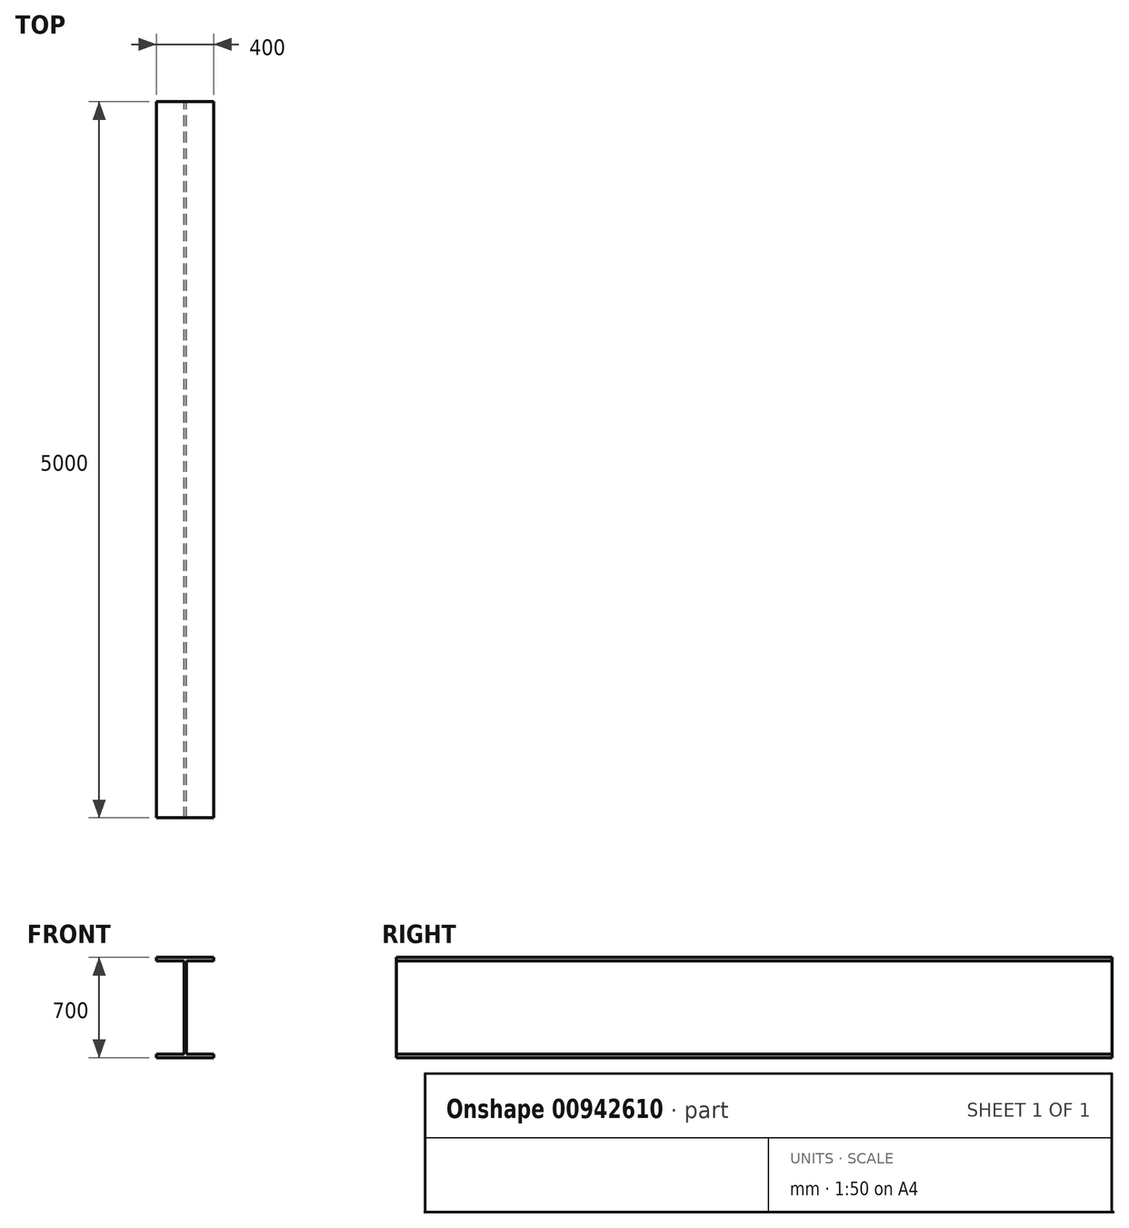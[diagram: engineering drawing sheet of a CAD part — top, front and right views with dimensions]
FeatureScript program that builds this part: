
annotation { "Feature Type Name" : "Feature", "Feature Type Description" : "" }
export const myFeature = defineFeature(function(context is Context, id is Id, definition is map)
    precondition{}
    {
        {
            var Q0;
            Q0=qCreatedBy(makeId("Front.planeOp"),FACE);
            var sketch = newSketch(context, id + "F0", { "sketchPlane" : qUnion([Q0])});
            skLineSegment(sketch, "E0.bottom", {"start": v(-253.34, 352.68) * mm, "end": v(146.66, 352.68) * mm});
            skLineSegment(sketch, "E0.top", {"start": v(-253.34, 327.68) * mm, "end": v(-61.34, 327.68) * mm});
            skLineSegment(sketch, "E0.left", {"start": v(-253.34, 352.68) * mm, "end": v(-253.34, 327.68) * mm});
            skLineSegment(sketch, "E0.right", {"start": v(146.66, 352.68) * mm, "end": v(146.66, 327.68) * mm});
            skLineSegment(sketch, "E1.bottom", {"start": v(-253.34, -322.32) * mm, "end": v(-61.34, -322.32) * mm});
            skLineSegment(sketch, "E1.top", {"start": v(-253.34, -347.32) * mm, "end": v(146.66, -347.32) * mm});
            skLineSegment(sketch, "E1.left", {"start": v(-253.34, -322.32) * mm, "end": v(-253.34, -347.32) * mm});
            skLineSegment(sketch, "E1.right", {"start": v(146.66, -322.32) * mm, "end": v(146.66, -347.32) * mm});
            skLineSegment(sketch, "E2", {"start": v(-53.34, 327.68) * mm, "end": v(-53.34, -322.32) * mm, "construction": true});
            skLineSegment(sketch, "E3", {"start": v(-61.34, 327.68) * mm, "end": v(-61.34, -322.32) * mm});
            skLineSegment(sketch, "E4", {"start": v(-45.34, 327.68) * mm, "end": v(-45.34, -322.32) * mm});
            skLineSegment(sketch, "E5.trimOffspring", {"start": v(-45.34, 327.68) * mm, "end": v(146.66, 327.68) * mm});
            skLineSegment(sketch, "E6.trimOffspring", {"start": v(-45.34, -322.32) * mm, "end": v(146.66, -322.32) * mm});
            skSolve(sketch);
        }
        {
            var Q0;
            Q0 = qSketchRegion(id + "F0", true);
            extrude(context, id + "F1", {"entities" : qUnion([Q0]), "depth" : 5000 * mm, "offsetDistance" : 25 * mm});
        }
    });
